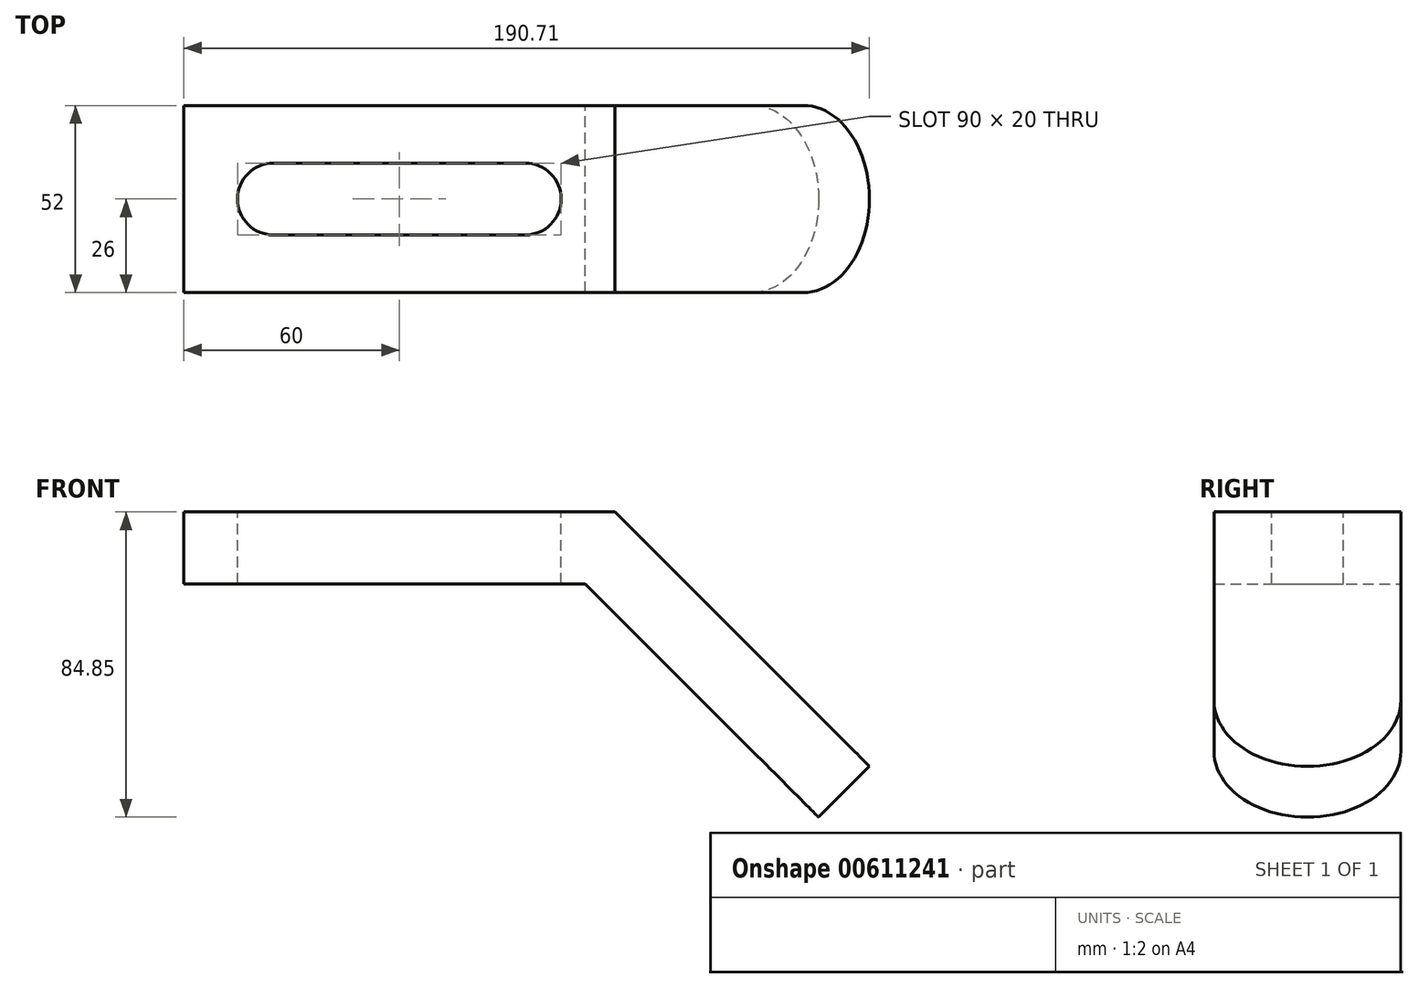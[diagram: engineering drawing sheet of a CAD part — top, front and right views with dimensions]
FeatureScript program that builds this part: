
annotation { "Feature Type Name" : "Feature", "Feature Type Description" : "" }
export const myFeature = defineFeature(function(context is Context, id is Id, definition is map)
    precondition{}
    {
        {
            var Q0;
            Q0=qCreatedBy(makeId("Front.planeOp"),FACE);
            var sketch = newSketch(context, id + "F0", { "sketchPlane" : qUnion([Q0])});
            skLineSegment(sketch, "E0", {"start": v(0, 0) * mm, "end": v(120, 0) * mm});
            skLineSegment(sketch, "E1", {"start": v(120, 0) * mm, "end": v(190.71, -70.71) * mm});
            skLineSegment(sketch, "E2", {"start": v(0, 0) * mm, "end": v(0, -20) * mm});
            skLineSegment(sketch, "E3", {"start": v(120, 0) * mm, "end": v(120, -20) * mm});
            skLineSegment(sketch, "E4", {"start": v(120, -20) * mm, "end": v(0, -20) * mm});
            skLineSegment(sketch, "E5", {"start": v(190.71, -70.71) * mm, "end": v(176.57, -84.85) * mm});
            skLineSegment(sketch, "E6", {"start": v(176.57, -84.85) * mm, "end": v(91.72, 0) * mm});
            skSolve(sketch);
        }
        {
            var Q0;
            {var subQ0=sQuery(id+"F0.wireOp",EDGE,"E2");Q0=makeQuery(id+"F0.imprint","IMPRINT",FACE,{"disambiguationData":[TD([[makeQuery(id+"F0.imprint","IMPRINT",EDGE,{"derivedFrom":subQ0}),1.0]])]});}
            var Q1;
            Q1=makeQuery(id+"F0.imprint","IMPRINT",FACE,{"disambiguationData":[TD([[makeQuery(id+"F0.imprint","IMPRINT",EDGE,{"derivedFrom":sQuery(id+"F0.wireOp",EDGE,"E1")}),-1.0]])]});
            var Q2;
            {var subQ0=sQuery(id+"F0.wireOp",EDGE,"E3");Q2=makeQuery(id+"F0.imprint","IMPRINT",FACE,{"disambiguationData":[TD([[makeQuery(id+"F0.imprint","IMPRINT",EDGE,{"derivedFrom":subQ0}),-1.0]])]});}
            extrude(context, id + "F1", {"entities" : qUnion([Q0, Q1, Q2]), "depth" : 52 * mm, "offsetDistance" : 25.4 * mm});
        }
        {
            var Q0;
            Q0=makeQuery(id+"F1.opExtrude","SWEPT_FACE",FACE,{"disambiguationData":[OSD([sQuery(id+"F0.wireOp",EDGE,"E0")])]});
            var sketch = newSketch(context, id + "F2", { "sketchPlane" : qUnion([Q0])});
            skLineSegment(sketch, "E7.bottom", {"start": v(25, -16) * mm, "end": v(95, -16) * mm});
            skLineSegment(sketch, "E7.top", {"start": v(25, -36) * mm, "end": v(95, -36) * mm});
            skLineSegment(sketch, "E7.left", {"start": v(25, -16) * mm, "end": v(25, -36) * mm});
            skLineSegment(sketch, "E7.right", {"start": v(95, -16) * mm, "end": v(95, -36) * mm});
            skSolve(sketch);
        }
        {
            var Q0;
            Q0=makeQuery(id+"F2.imprint","IMPRINT",FACE,{"disambiguationData":[TD([[makeQuery(id+"F2.imprint","IMPRINT",EDGE,{"derivedFrom":sQuery(id+"F2.wireOp",EDGE,"E7.bottom")}),1.0]])]});
            var sketch = newSketch(context, id + "F3", { "sketchPlane" : qUnion([Q0])});
            skCircle(sketch, "E8", {"center": v(25, -26) * mm, "radius": 10 * mm});
            skSolve(sketch);
        }
        {
            var Q0;
            Q0=makeQuery(id+"F2.imprint","IMPRINT",FACE,{"disambiguationData":[TD([[makeQuery(id+"F2.imprint","IMPRINT",EDGE,{"derivedFrom":sQuery(id+"F2.wireOp",EDGE,"E7.bottom")}),1.0]])]});
            var sketch = newSketch(context, id + "F4", { "sketchPlane" : qUnion([Q0])});
            skCircle(sketch, "E9", {"center": v(95, -26) * mm, "radius": 10 * mm});
            skSolve(sketch);
        }
        {
            var Q0;
            Q0=makeQuery(id+"F2.imprint","IMPRINT",FACE,{"disambiguationData":[TD([[makeQuery(id+"F2.imprint","IMPRINT",EDGE,{"derivedFrom":sQuery(id+"F2.wireOp",EDGE,"E7.bottom")}),-1.0]])]});
            var Q1;
            {var subQ1=makeQuery(id+"F2.imprint","IMPRINT",EDGE,{"derivedFrom":sQuery(id+"F2.wireOp",EDGE,"E7.right")});Q1=makeQuery(id+"F4.imprint","IMPRINT",FACE,{"disambiguationData":[TD([[makeQuery(id+"F4.imprint","IMPRINT",EDGE,{"derivedFrom":subQ1}),1.0]])]});}
            var Q2;
            {var subQ1=makeQuery(id+"F2.imprint","IMPRINT",EDGE,{"derivedFrom":sQuery(id+"F2.wireOp",EDGE,"E7.left")});Q2=makeQuery(id+"F3.imprint","IMPRINT",FACE,{"disambiguationData":[TD([[makeQuery(id+"F3.imprint","IMPRINT",EDGE,{"derivedFrom":subQ1}),-1.0]])]});}
            extrude(context, id + "F5", {"entities" : qUnion([Q0, Q1, Q2]), "operationType" : NewBodyOperationType.REMOVE, "oppositeDirection" : true, "depth" : 20 * mm, "offsetDistance" : 25.4 * mm});
        }
        {
            var Q0;
            Q0=makeQuery(id+"F1.opExtrude","SWEPT_FACE",FACE,{"disambiguationData":[OSD([sQuery(id+"F0.wireOp",EDGE,"E1")])]});
            var sketch = newSketch(context, id + "F6", { "sketchPlane" : qUnion([Q0])});
            skCircle(sketch, "E10", {"center": v(158.85, -26) * mm, "radius": 10 * mm});
            skSolve(sketch);
        }
        {
            var Q0;
            Q0=makeQuery(id+"F6.imprint","IMPRINT",FACE,{"disambiguationData":[TD([[makeQuery(id+"F6.imprint","IMPRINT",EDGE,{"derivedFrom":sQuery(id+"F6.wireOp",EDGE,"E10")}),1.0]])]});
            extrude(context, id + "F7", {"entities" : qUnion([Q0]), "operationType" : NewBodyOperationType.REMOVE, "oppositeDirection" : true, "depth" : 20 * mm, "offsetDistance" : 25.4 * mm});
        }
        {
            var Q0;
            Q0=makeQuery(id+"F1.opExtrude","CAP_EDGE",EDGE,{"disambiguationData":[OSD([sQuery(id+"F0.wireOp",EDGE,"E5")])],"isStart":false});
            fillet(context, id + "F8", {"entities" : qUnion([Q0]), "radius" : 26 * mm, "tangentPropagation" : true, "allowEdgeOverflow" : false});
        }
        {
            var Q0;
            Q0=makeQuery(id+"F1.opExtrude","CAP_EDGE",EDGE,{"disambiguationData":[OSD([sQuery(id+"F0.wireOp",EDGE,"E5")])],"isStart":true});
            fillet(context, id + "F9", {"entities" : qUnion([Q0]), "radius" : 26 * mm, "tangentPropagation" : true, "allowEdgeOverflow" : false});
        }
    });
